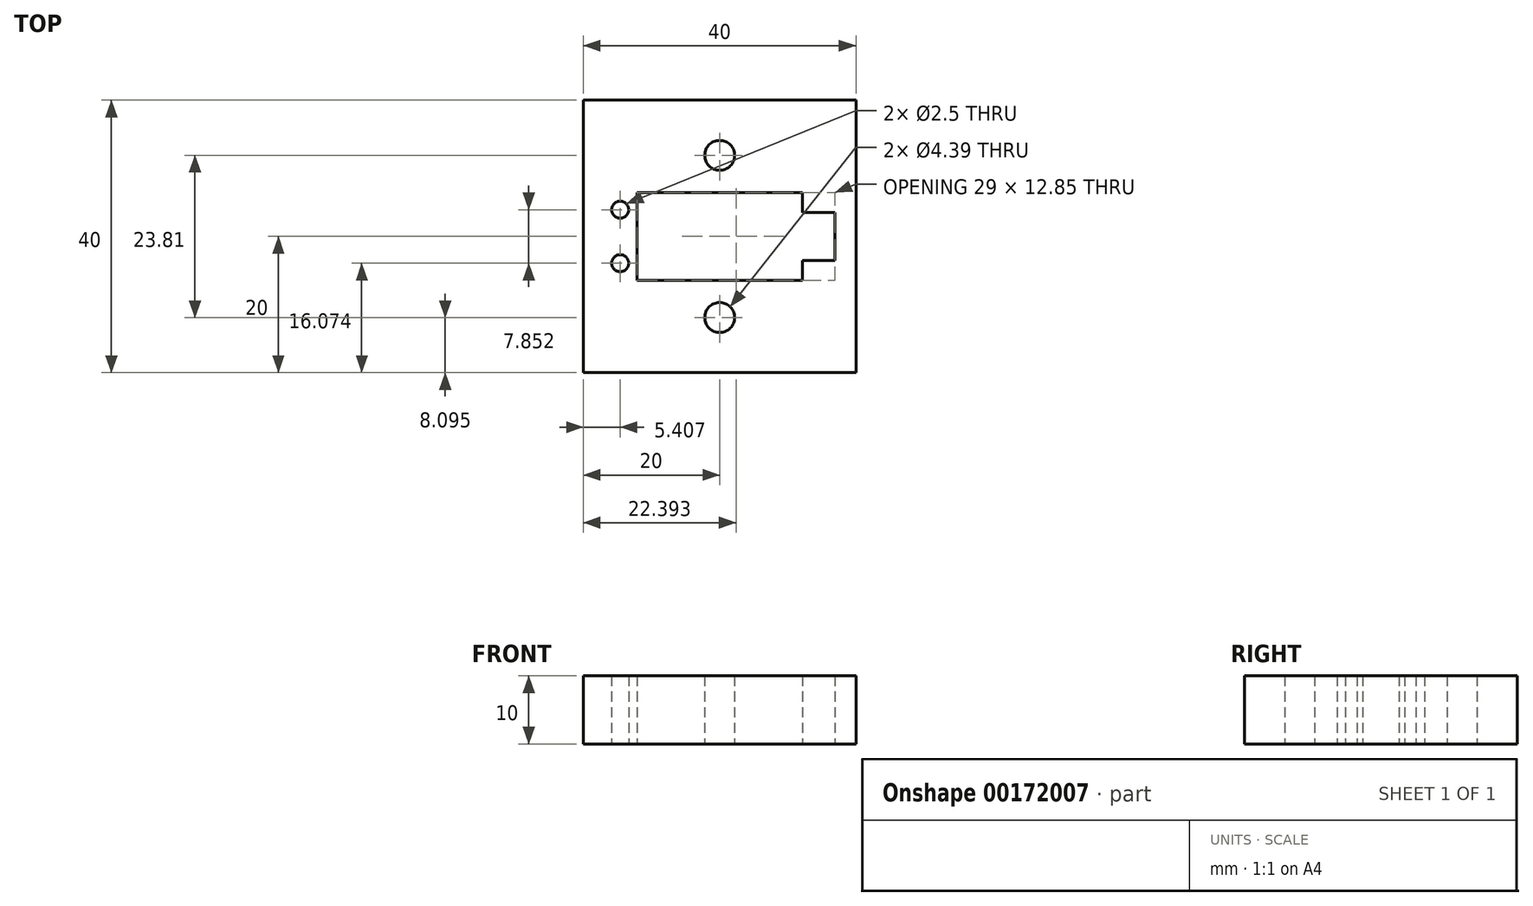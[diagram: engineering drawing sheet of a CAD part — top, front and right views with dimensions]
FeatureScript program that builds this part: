
annotation { "Feature Type Name" : "Feature", "Feature Type Description" : "" }
export const myFeature = defineFeature(function(context is Context, id is Id, definition is map)
    precondition{}
    {
        {
            var Q0;
            Q0=qCreatedBy(makeId("Top.planeOp"),FACE);
            var sketch = newSketch(context, id + "F0", { "sketchPlane" : qUnion([Q0])});
            skLineSegment(sketch, "E0.bottom", {"start": v(0, 0) * mm, "end": v(40, 0) * mm});
            skLineSegment(sketch, "E0.top", {"start": v(0, 40) * mm, "end": v(40, 40) * mm});
            skLineSegment(sketch, "E0.left", {"start": v(0, 0) * mm, "end": v(0, 40) * mm});
            skLineSegment(sketch, "E0.right", {"start": v(40, 0) * mm, "end": v(40, 40) * mm});
            skCircle(sketch, "E1", {"center": v(20, 31.9) * mm, "radius": 2.2 * mm});
            skCircle(sketch, "E2", {"center": v(20, 8.1) * mm, "radius": 2.2 * mm});
            skLineSegment(sketch, "E3.bottom", {"start": v(7.9, 26.43) * mm, "end": v(32.1, 26.43) * mm});
            skLineSegment(sketch, "E3.top", {"start": v(7.9, 13.57) * mm, "end": v(32.1, 13.57) * mm});
            skLineSegment(sketch, "E3.left", {"start": v(7.9, 26.43) * mm, "end": v(7.9, 13.57) * mm});
            skLineSegment(sketch, "E3.right", {"start": v(32.1, 26.43) * mm, "end": v(32.1, 23.5) * mm});
            skLineSegment(sketch, "E4", {"start": v(20, 31.9) * mm, "end": v(20, 40) * mm, "construction": true});
            skLineSegment(sketch, "E5", {"start": v(20, 8.1) * mm, "end": v(20, 0) * mm, "construction": true});
            skLineSegment(sketch, "E6", {"start": v(20, 0) * mm, "end": v(20, 40) * mm, "construction": true});
            skLineSegment(sketch, "E7", {"start": v(20, 26.43) * mm, "end": v(20, 13.57) * mm, "construction": true});
            skLineSegment(sketch, "E8", {"start": v(7.9, 20) * mm, "end": v(32.1, 20) * mm, "construction": true});
            skLineSegment(sketch, "E9", {"start": v(0, 20) * mm, "end": v(40, 20) * mm, "construction": true});
            skLineSegment(sketch, "E10.bottom", {"start": v(32.1, 23.5) * mm, "end": v(36.9, 23.5) * mm});
            skLineSegment(sketch, "E10.top", {"start": v(32.1, 16.5) * mm, "end": v(36.9, 16.5) * mm});
            skLineSegment(sketch, "E10.right", {"start": v(36.9, 23.5) * mm, "end": v(36.9, 16.5) * mm});
            skLineSegment(sketch, "E11", {"start": v(36.9, 20) * mm, "end": v(32.1, 20) * mm, "construction": true});
            skLineSegment(sketch, "E12.trimOffspring", {"start": v(32.1, 16.5) * mm, "end": v(32.1, 13.57) * mm});
            skLineSegment(sketch, "E13", {"start": v(5.4, 23.93) * mm, "end": v(5.4, 16.07) * mm, "construction": true});
            skCircle(sketch, "E14", {"center": v(5.4, 23.93) * mm, "radius": 1.25 * mm});
            skCircle(sketch, "E15", {"center": v(5.4, 16.07) * mm, "radius": 1.25 * mm});
            skSolve(sketch);
        }
        {
            var Q0;
            Q0 = qSketchRegion(id + "F0", true);
            extrude(context, id + "F1", {"entities" : qUnion([Q0]), "depth" : 10 * mm});
        }
    });
